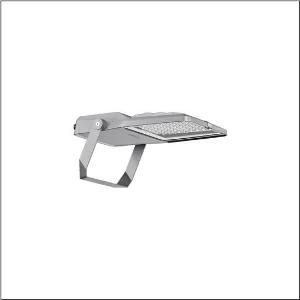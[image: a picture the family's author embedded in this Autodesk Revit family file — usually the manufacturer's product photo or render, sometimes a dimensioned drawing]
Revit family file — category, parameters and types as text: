
# Revit family: floodlight_fl_21_iq_mini___pl52_5xa7772b3d1a_2253
name_source: partatom
category: Lighting Fixtures
units: mm (PartAtom-declared; Revit-internal decimal feet)

## family parameters
Cut with Voids When Loaded = No
Host = Face
Light Source = No
Part Type = Normal
Room Calculation Point = No
Round Connector Dimension = Use Diameter
Shared = No

## types (1)
- --- (1 x LED, 5370 lm, 45.5 W, 3000K)
    Apparent Load = 46 VA
    CIE Flux Codes = 26 60 98 100 100
    Color Rendering = 80
    Color Temperature = 3000K
    Default Elevation = 1800 mm
    Description = Floodlight FL 21 iQ mini, floodlight, primary light control with lens, of PMMA, primary optical cover: protective disc, of toughened safety glass, transparent, light distribution: PL52, light emission: direct distribution, installation type: surface-mounted, LED, High Power LED, rated luminous flux: 5.370lm, luminous efficacy: 118lm/W, light colour: 830, colour temperature: 3000K, control: Street-Remote, Auto-Match, Temp-Guard, Night-Set, Smart-Wire, Desk-Remote (wireless, voltage-free reading and setting of iQ features in the workshop via application-optimized NFC function/RFID function), optimised constant luminous flux control (CLO 2.0), with terminal, 6-pole, mains connection: 220..240V, AC, 50/60Hz, start of lifetime: 46W, end of service life: 48W, reduction: 21W, luminaire housing, of diecast aluminium, powder-coated, Siteco® metallic grey (DB 702S), corrosivity category C5 mid according to DIN EN ISO 12944, sealing non-destructively replaceable, mounting bracket, of steel, galvanised, powder-coated, Siteco® metallic grey (DB 702S), protection rating (complete): IP66, insulation class (complete): insulation class II (safety insulation), certification: CE, ENEC, VDE, protection symbol: D, impact resistance: IK08, permissible operating ambient temperature: -40..+40°C, permissible operating ambient temperature for outdoor applications: -40..+50°C, standard: DIN EN 12944, LABS conformity tested according to VDMA 24364:2018-05, packaging unit: 1 piece

Light Distribution: PL52
    Height = 70 mm
    Lamp = 1 x LED
    Lamp Light Flux = 5370 lm
    Lamp Power = 45.5 W
    Lamp count = 1
    Length = 485 mm
    Luminous efficacy = 118 lm/W
    Manufacturer = Siteco
    ModVariant = No
    Model = 5XA7772B3D1A
    Number of Poles = 1
    OnlyDefault = Yes
    Power Factor = 1
    Product Name = Floodlight FL 21 iQ mini | PL52
    Product group = floodlight | pylon annexe
    ProductGroupID = 6200
    Protection Class = Protection class II
    Protection Degree = IP 66
    RLX_Detail_Level = 1
    RLX_Emergency_Light_Flux = 0 lm
    RLX_Emergency_Type = 0
    RLX_Emergency_Type_DB = No
    RlxData = <blob elided: 96285 chars, md5=c1c2d74b>
    Socket = socket
    Standby Power = 0 W
    System Light Flux = 5370 lm
    System Power = 46 W
    Type Comments = factory setting: luminous flux: 100 % | dim-lin: 254 | 463 mA
    Type Image = l_1006845.jpg
    URL = http://relux.com
    VarID = @adj_097107
    Voltage = 0 V
    Weight = 0.00 kg
    Width = 337 mm

## geometry (parser evidence)
native form markers: Blend x4, Sweep x12
no freeform markers — native parametric forms only
